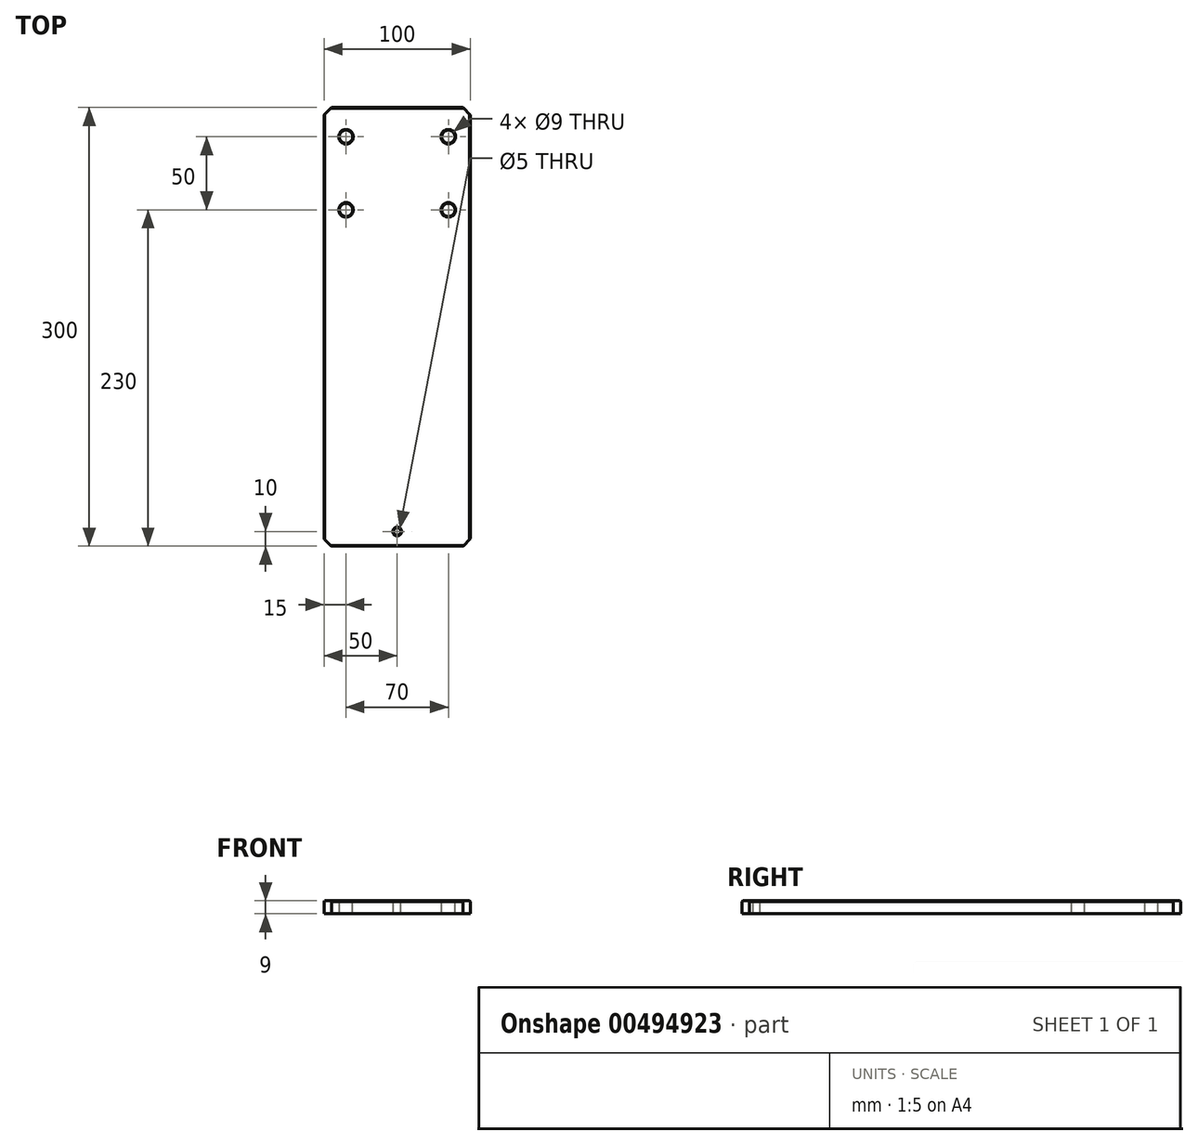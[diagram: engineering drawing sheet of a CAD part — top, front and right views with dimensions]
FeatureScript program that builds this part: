
annotation { "Feature Type Name" : "Feature", "Feature Type Description" : "" }
export const myFeature = defineFeature(function(context is Context, id is Id, definition is map)
    precondition{}
    {
        {
            var Q0;
            Q0=qCreatedBy(makeId("Top.planeOp"),FACE);
            var sketch = newSketch(context, id + "F0", { "sketchPlane" : qUnion([Q0])});
            skLineSegment(sketch, "E0.bottom", {"start": v(0, 0) * mm, "end": v(-100, 0) * mm});
            skLineSegment(sketch, "E0.top", {"start": v(0, 300) * mm, "end": v(-100, 300) * mm});
            skLineSegment(sketch, "E0.left", {"start": v(0, 0) * mm, "end": v(0, 300) * mm});
            skLineSegment(sketch, "E0.right", {"start": v(-100, 0) * mm, "end": v(-100, 300) * mm});
            skSolve(sketch);
        }
        {
            var Q0;
            Q0=qSketchRegion(id+"F0",true);
            extrude(context, id + "F1", {"entities" : qUnion([Q0]), "depth" : 9 * mm});
        }
        {
            var Q0;
            Q0=makeQuery(id+"F1.opExtrude","CAP_FACE",FACE,{"disambiguationData":[OSD([sQuery(id+"F0.wireOp",EDGE,"E0.bottom"),sQuery(id+"F0.wireOp",EDGE,"E0.top"),sQuery(id+"F0.wireOp",EDGE,"E0.left"),sQuery(id+"F0.wireOp",EDGE,"E0.right")])],"isStart":false});
            var sketch = newSketch(context, id + "F2", { "sketchPlane" : qUnion([Q0])});
            skPoint(sketch, "E1", {"position": v(-85, 280) * mm});
            skPoint(sketch, "E2", {"position": v(-15, 280) * mm});
            skPoint(sketch, "E3", {"position": v(-15, 230) * mm});
            skPoint(sketch, "E4", {"position": v(-85, 230) * mm});
            skSolve(sketch);
        }
        {
            var Q0;
            Q0=sQuery(id+"F2.wireOp",VERTEX,"E1");
            var Q1;
            Q1=sQuery(id+"F2.wireOp",VERTEX,"E2");
            var Q2;
            Q2=sQuery(id+"F2.wireOp",VERTEX,"E3");
            var Q3;
            Q3=sQuery(id+"F2.wireOp",VERTEX,"E4");
            var Q4;
            Q4=makeQuery(id+"F1.opExtrude","SWEPT_BODY",BODY,{"disambiguationData":[OSD([sQuery(id+"F0.wireOp",EDGE,"E0.bottom"),sQuery(id+"F0.wireOp",EDGE,"E0.top"),sQuery(id+"F0.wireOp",EDGE,"E0.left"),sQuery(id+"F0.wireOp",EDGE,"E0.right")])]});
            hole(context, id + "F3", {"style" : HoleStyle.SIMPLE, "endStyle" : HoleEndStyle.THROUGH, "holeDiameter" : 9 * mm, "isTappedThrough" : true, "tappedDepth" : 7.9 * mm, "tapClearance" : 3, "locations" : qUnion([Q0, Q1, Q2, Q3]), "scope" : qUnion([Q4])});
        }
        {
            var Q0;
            Q0=makeQuery(id+"F1.opExtrude","CAP_FACE",FACE,{"disambiguationData":[OSD([sQuery(id+"F0.wireOp",EDGE,"E0.bottom"),sQuery(id+"F0.wireOp",EDGE,"E0.top"),sQuery(id+"F0.wireOp",EDGE,"E0.left"),sQuery(id+"F0.wireOp",EDGE,"E0.right")])],"isStart":false});
            var sketch = newSketch(context, id + "F4", { "sketchPlane" : qUnion([Q0])});
            skPoint(sketch, "E5", {"position": v(-50, 10) * mm});
            skSolve(sketch);
        }
        {
            var Q0;
            Q0=sQuery(id+"F4.wireOp",VERTEX,"E5");
            var Q1;
            Q1=makeQuery(id+"F1.opExtrude","SWEPT_BODY",BODY,{"disambiguationData":[OSD([sQuery(id+"F0.wireOp",EDGE,"E0.bottom"),sQuery(id+"F0.wireOp",EDGE,"E0.top"),sQuery(id+"F0.wireOp",EDGE,"E0.left"),sQuery(id+"F0.wireOp",EDGE,"E0.right")])]});
            hole(context, id + "F5", {"style" : HoleStyle.SIMPLE, "endStyle" : HoleEndStyle.THROUGH, "standardTappedOrClearance" : lookupTablePath({ "standard" : "ISO", "engagement" : "75%", "pitch" : "1 mm", "size" : "M6", "type" : "Tapped" }), "standardBlindInLast" : lookupTablePath({ "standard" : "ISO", "engagement" : "75%", "pitch" : "1 mm", "size" : "M6", "type" : "Tapped" }), "holeDiameter" : 5 * mm, "showTappedDepth" : true, "isTappedThrough" : true, "tappedDepth" : 7.9 * mm, "tapClearance" : 3, "locations" : qUnion([Q0]), "scope" : qUnion([Q1]), "majorDiameter" : 6 * mm});
        }
        {
            var Q0;
            Q0=makeQuery(id+"F1.opExtrude","CAP_FACE",FACE,{"disambiguationData":[OSD([sQuery(id+"F0.wireOp",EDGE,"E0.bottom"),sQuery(id+"F0.wireOp",EDGE,"E0.top"),sQuery(id+"F0.wireOp",EDGE,"E0.left"),sQuery(id+"F0.wireOp",EDGE,"E0.right")])],"isStart":false});
            var Q1;
            Q1=makeQuery(id+"F5.hole-0.boolean.opBoolean","INTERSECT",EDGE,{"derivedFrom":[makeQuery(id+"F1.opExtrude","CAP_FACE",FACE,{"disambiguationData":[OSD([sQuery(id+"F0.wireOp",EDGE,"E0.bottom"),sQuery(id+"F0.wireOp",EDGE,"E0.top"),sQuery(id+"F0.wireOp",EDGE,"E0.left"),sQuery(id+"F0.wireOp",EDGE,"E0.right")])],"isStart":true}),makeQuery(id+"F5.hole-0.opRevolve","SWEPT_FACE",FACE,{"disambiguationData":[OSD([sQuery(id+"F5.hole-0.sketch.wireOp",EDGE,"core_line_2")])]})]});
            chamfer(context, id + "F6", {"entities" : qUnion([Q0, Q1]), "width" : 0.5 * mm, "tangentPropagation" : true});
        }
        {
            var Q0;
            Q0=makeQuery(id+"F1.opExtrude","SWEPT_EDGE",EDGE,{"disambiguationData":[OSD([sQuery(id+"F0.wireOp",EDGE,"E0.bottom"),sQuery(id+"F0.wireOp",EDGE,"E0.right")])]});
            var Q1;
            Q1=makeQuery(id+"F1.opExtrude","SWEPT_EDGE",EDGE,{"disambiguationData":[OSD([sQuery(id+"F0.wireOp",EDGE,"E0.bottom"),sQuery(id+"F0.wireOp",EDGE,"E0.left")])]});
            var Q2;
            Q2=makeQuery(id+"F1.opExtrude","SWEPT_EDGE",EDGE,{"disambiguationData":[OSD([sQuery(id+"F0.wireOp",EDGE,"E0.top"),sQuery(id+"F0.wireOp",EDGE,"E0.right")])]});
            var Q3;
            Q3=makeQuery(id+"F1.opExtrude","SWEPT_EDGE",EDGE,{"disambiguationData":[OSD([sQuery(id+"F0.wireOp",EDGE,"E0.top"),sQuery(id+"F0.wireOp",EDGE,"E0.left")])]});
            chamfer(context, id + "F7", {"entities" : qUnion([Q0, Q1, Q2, Q3]), "width" : 5 * mm, "tangentPropagation" : true});
        }
    });
